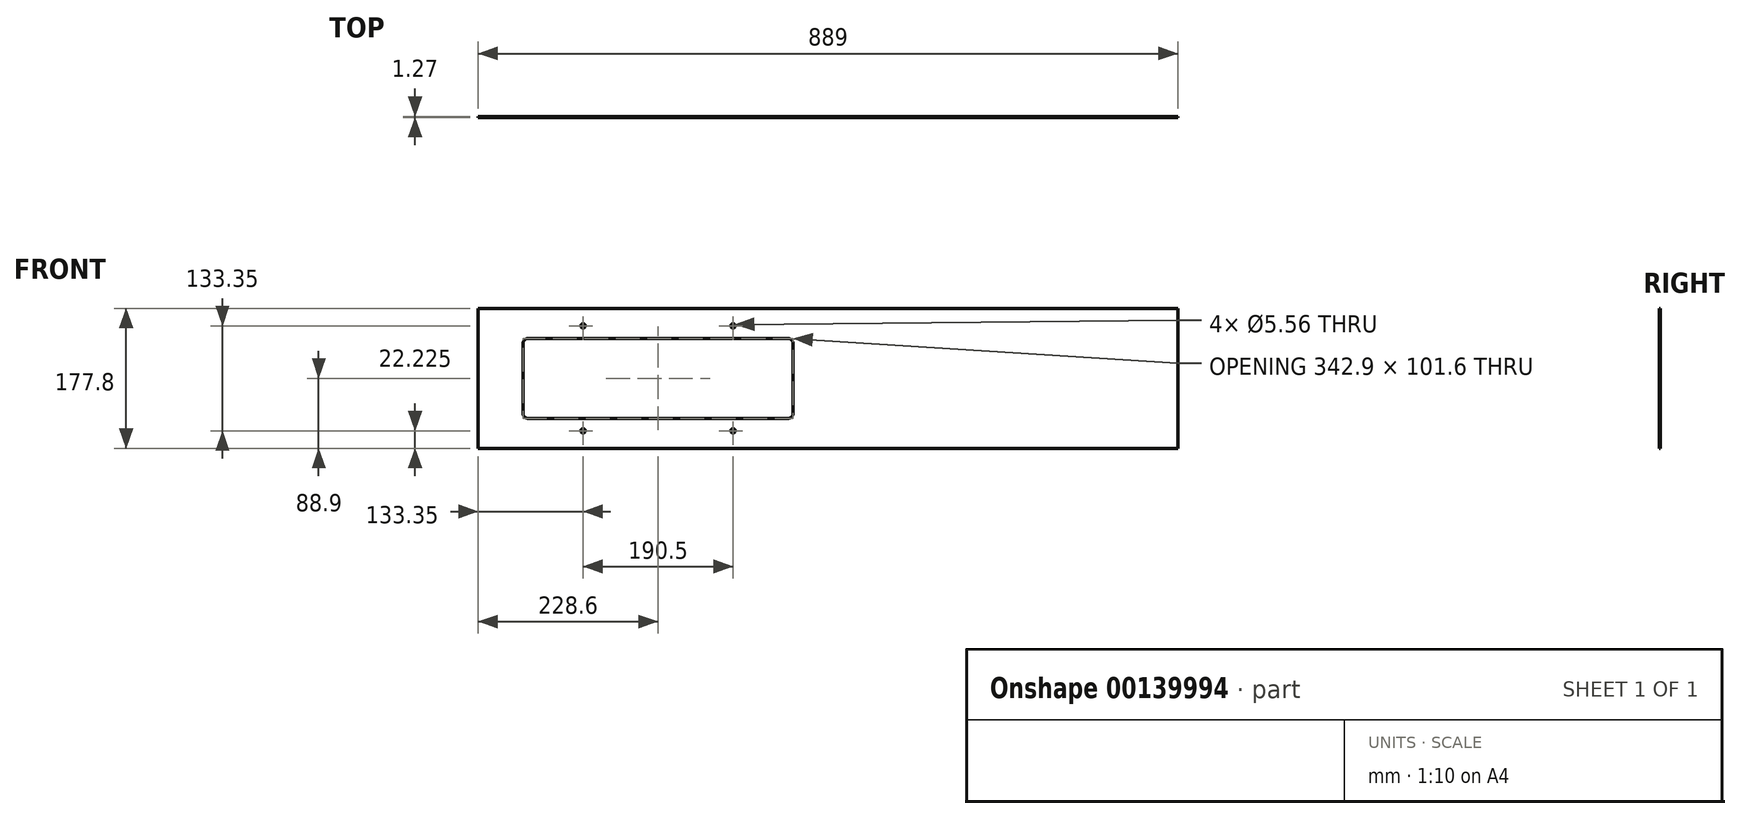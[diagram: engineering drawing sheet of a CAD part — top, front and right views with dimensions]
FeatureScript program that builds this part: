
annotation { "Feature Type Name" : "Feature", "Feature Type Description" : "" }
export const myFeature = defineFeature(function(context is Context, id is Id, definition is map)
    precondition{}
    {
        {
            var Q0;
            Q0=qCreatedBy(makeId("Front.planeOp"),FACE);
            var sketch = newSketch(context, id + "F0", { "sketchPlane" : qUnion([Q0])});
            skLineSegment(sketch, "E0.bottom", {"start": v(444.5, 88.9) * mm, "end": v(-444.5, 88.9) * mm});
            skLineSegment(sketch, "E0.top", {"start": v(444.5, -88.9) * mm, "end": v(-444.5, -88.9) * mm});
            skLineSegment(sketch, "E0.left", {"start": v(444.5, 88.9) * mm, "end": v(444.5, -88.9) * mm});
            skLineSegment(sketch, "E0.right", {"start": v(-444.5, 88.9) * mm, "end": v(-444.5, -88.9) * mm});
            skPoint(sketch, "E0.middle", {"position": v(0, 0) * mm});
            skLineSegment(sketch, "E1.bottom", {"start": v(-50.8, 50.8) * mm, "end": v(-381, 50.8) * mm});
            skLineSegment(sketch, "E1.top", {"start": v(-50.8, -50.8) * mm, "end": v(-381, -50.8) * mm});
            skLineSegment(sketch, "E1.left", {"start": v(-44.45, 44.45) * mm, "end": v(-44.45, -44.45) * mm});
            skLineSegment(sketch, "E1.right", {"start": v(-387.35, 44.45) * mm, "end": v(-387.35, -44.45) * mm});
            skPoint(sketch, "E1.middle", {"position": v(-215.9, 0) * mm});
            skCircle(sketch, "E2", {"center": v(-311.15, -66.68) * mm, "radius": 2.78 * mm});
            skCircle(sketch, "E3.0.1.0", {"center": v(-311.15, 66.68) * mm, "radius": 2.78 * mm});
            skCircle(sketch, "E3.1.0.0", {"center": v(-120.65, -66.68) * mm, "radius": 2.78 * mm});
            skCircle(sketch, "E3.1.1.0", {"center": v(-120.65, 66.68) * mm, "radius": 2.78 * mm});
            skLineSegment(sketch, "E3.direction1", {"start": v(-311.15, -66.68) * mm, "end": v(-120.65, -66.68) * mm, "construction": true});
            skLineSegment(sketch, "E3.direction2", {"start": v(-311.15, -66.68) * mm, "end": v(-311.15, 66.68) * mm, "construction": true});
            skLineSegment(sketch, "E4", {"start": v(-311.15, 0) * mm, "end": v(0, 0) * mm, "construction": true});
            skPoint(sketch, "E5.visualSharp", {"position": v(-44.45, 50.8) * mm});
            skArc(sketch, "E5.filletArc", {"start": v(-44.45, 44.45) * mm, "mid": v(-46.3, 48.94) * mm, "end": v(-50.8, 50.8) * mm});
            skPoint(sketch, "E6.visualSharp", {"position": v(-387.35, 50.8) * mm});
            skArc(sketch, "E6.filletArc", {"start": v(-381, 50.8) * mm, "mid": v(-385.5, 48.94) * mm, "end": v(-387.35, 44.45) * mm});
            skPoint(sketch, "E7.visualSharp", {"position": v(-387.35, -50.8) * mm});
            skArc(sketch, "E7.filletArc", {"start": v(-387.35, -44.45) * mm, "mid": v(-385.5, -48.94) * mm, "end": v(-381, -50.8) * mm});
            skPoint(sketch, "E8.visualSharp", {"position": v(-44.45, -50.8) * mm});
            skArc(sketch, "E8.filletArc", {"start": v(-50.8, -50.8) * mm, "mid": v(-46.3, -48.94) * mm, "end": v(-44.45, -44.45) * mm});
            skSolve(sketch);
        }
        {
            var Q0;
            Q0=makeQuery(id+"F0.imprint","IMPRINT",FACE,{"disambiguationData":[TD([[makeQuery(id+"F0.imprint","IMPRINT",EDGE,{"derivedFrom":sQuery(id+"F0.wireOp",EDGE,"E0.bottom")}),1.0]])]});
            extrude(context, id + "F1", {"entities" : qUnion([Q0]), "depth" : 1.27 * mm});
        }
    });
